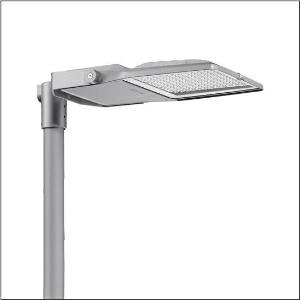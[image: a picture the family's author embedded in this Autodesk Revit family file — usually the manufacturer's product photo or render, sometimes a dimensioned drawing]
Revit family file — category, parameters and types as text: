
# Revit family: floodlight_fl_21_midi___pl33t_5xa7786f2f3a_5712
name_source: partatom
category: Lighting Fixtures
units: mm (PartAtom-declared; Revit-internal decimal feet)

## family parameters
Cut with Voids When Loaded = No
Host = Face
Light Source = No
Part Type = Normal
Room Calculation Point = No
Round Connector Dimension = Use Diameter
Shared = No

## types (1)
- --- (1 x LED, 35340 lm, 271.6 W, 3000K)
    Apparent Load = 272 VA
    CIE Flux Codes = 26 75 99 100 100
    Color Rendering = 70
    Color Temperature = 3000K
    Default Elevation = 1800 mm
    Description = Floodlight FL 21 midi, floodlight, primary light control with lens, of PMMA, primary optical cover: protective disc, of toughened safety glass, transparent, light distribution: PL33T, light emission: direct distribution, installation type: surface-mounted, LED, High Power LED, rated luminous flux: 35.340lm, luminous efficacy: 130lm/W, light colour: 730, colour temperature: 3000K, control gear: ECG Smart Interface, control: flexible luminous flux parameterisation, time-dependent luminous flux control, constant luminous flux control, overheat protection, pre-setting: logarithmic dimming characteristic, with terminal, 6-pole, mains connection: 220..240V, AC, 50/60Hz, start of lifetime: 272W, end of service life: 287W, reduction: 123W, luminaire housing, of diecast aluminium, powder-coated, Siteco® metallic grey (DB 702S), corrosivity category C5 mid according to DIN EN ISO 12944, sealing non-destructively replaceable, please order mast flange separately, mast bracket, of steel, galvanised, powder-coated, Siteco® metallic grey (DB 702S), Smart Interface below and above, protection rating (complete): IP66, insulation class (complete): insulation class II (safety insulation), certification: CE, ENEC, VDE, protection symbol: D, impact resistance: IK08, permissible operating ambient temperature: -40..+40°C, permissible operating ambient temperature for outdoor applications: -40..+50°C, standard: DIN EN 12944, LABS conformity tested according to VDMA 24364:2018-05, packaging unit: 1 piece

Light Distribution: PL33T
    Height = 76 mm
    Lamp = 1 x LED
    Lamp Light Flux = 35340 lm
    Lamp Power = 271.6 W
    Lamp count = 1
    Length = 657 mm
    Luminous efficacy = 130 lm/W
    Manufacturer = Siteco
    ModVariant = No
    Model = 5XA7786F2F3A
    Number of Poles = 1
    OnlyDefault = Yes
    Power Factor = 1
    Product Name = Floodlight FL 21 midi | PL33T
    Product group = floodlight | pylon annexe
    ProductGroupID = 6200
    Protection Class = Protection class II
    Protection Degree = IP 66
    RLX_Detail_Level = 1
    RLX_Emergency_Light_Flux = 0 lm
    RLX_Emergency_Type = 0
    RLX_Emergency_Type_DB = No
    RlxData = <blob elided: 153661 chars, md5=748e75bb>
    Socket = socket
    Standby Power = 0 W
    System Light Flux = 35340 lm
    System Power = 272 W
    Type Comments = factory setting: luminous flux: 100 % | dim-lin: 254 | 620 mA
    Type Image = l_1007123.jpg
    URL = http://relux.com
    VarID = @adj_120725
    Voltage = 0 V
    Weight = 0.00 kg
    Width = 442 mm

## geometry (parser evidence)
native form markers: Blend x4, Sweep x12
no freeform markers — native parametric forms only
